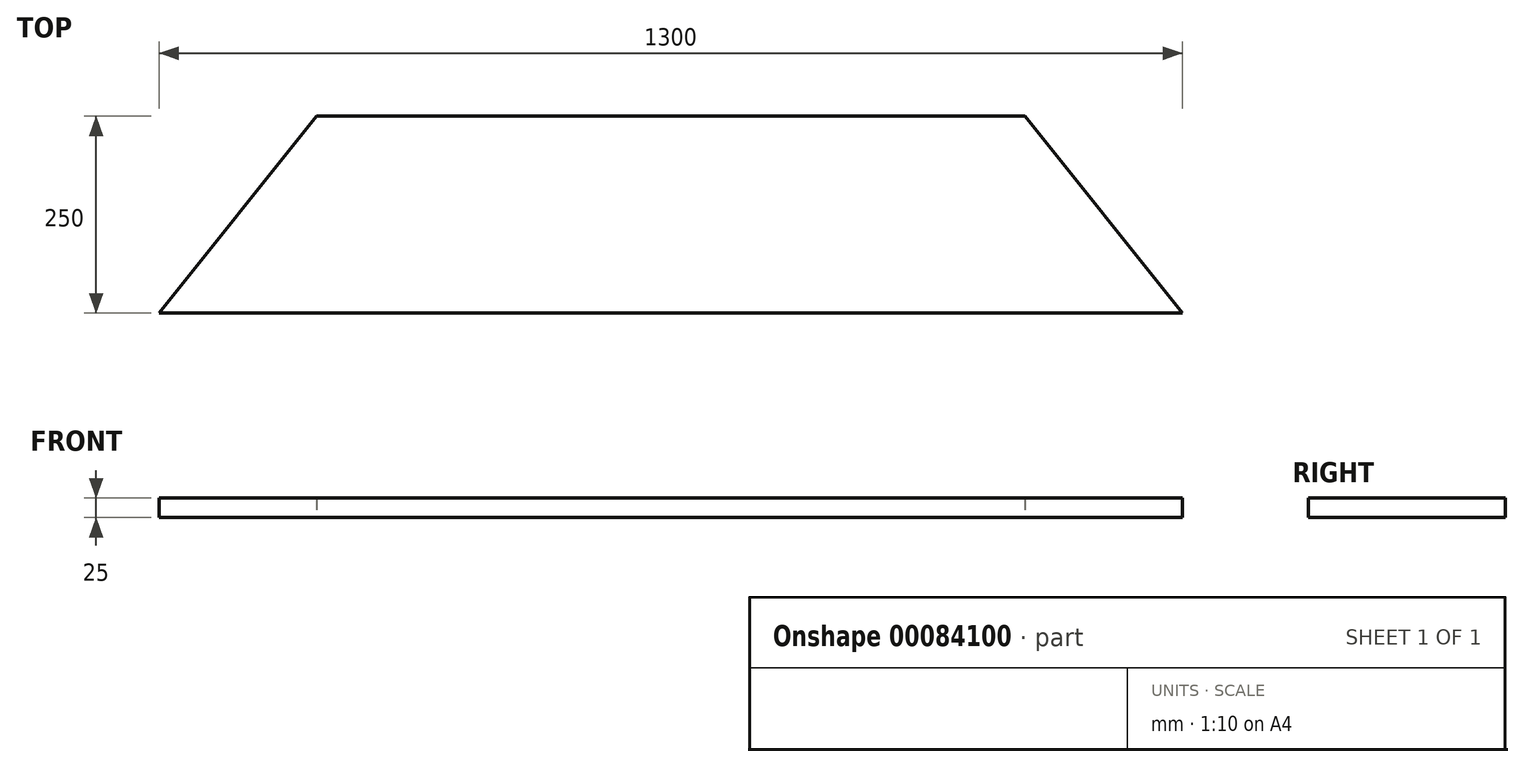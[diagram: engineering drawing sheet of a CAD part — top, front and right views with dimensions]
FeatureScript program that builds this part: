
annotation { "Feature Type Name" : "Feature", "Feature Type Description" : "" }
export const myFeature = defineFeature(function(context is Context, id is Id, definition is map)
    precondition{}
    {
        {
            var Q0;
            Q0=qCreatedBy(makeId("Top.planeOp"),FACE);
            var sketch = newSketch(context, id + "F0", { "sketchPlane" : qUnion([Q0])});
            skLineSegment(sketch, "E0", {"start": v(-1001.05, 490.83) * mm, "end": v(-801.05, 740.83) * mm});
            skLineSegment(sketch, "E1", {"start": v(-801.05, 740.83) * mm, "end": v(98.95, 740.83) * mm});
            skLineSegment(sketch, "E2", {"start": v(98.95, 740.83) * mm, "end": v(298.95, 490.83) * mm});
            skLineSegment(sketch, "E3", {"start": v(298.95, 490.83) * mm, "end": v(-1001.05, 490.83) * mm});
            skPoint(sketch, "E4", {"position": v(-351.05, 740.83) * mm});
            skLineSegment(sketch, "E5", {"start": v(-351.05, 811.09) * mm, "end": v(-351.05, -704.77) * mm, "construction": true});
            skPoint(sketch, "E6", {"position": v(-351.05, 490.83) * mm});
            skSolve(sketch);
        }
        {
            var Q0;
            Q0=makeQuery(id+"F0.imprint","IMPRINT",FACE,{"disambiguationData":[TD([[makeQuery(id+"F0.imprint","IMPRINT",EDGE,{"derivedFrom":sQuery(id+"F0.wireOp",EDGE,"E0")}),-1.0]])]});
            extrude(context, id + "F1", {"entities" : qUnion([Q0]), "depth" : 25 * mm});
        }
    });
